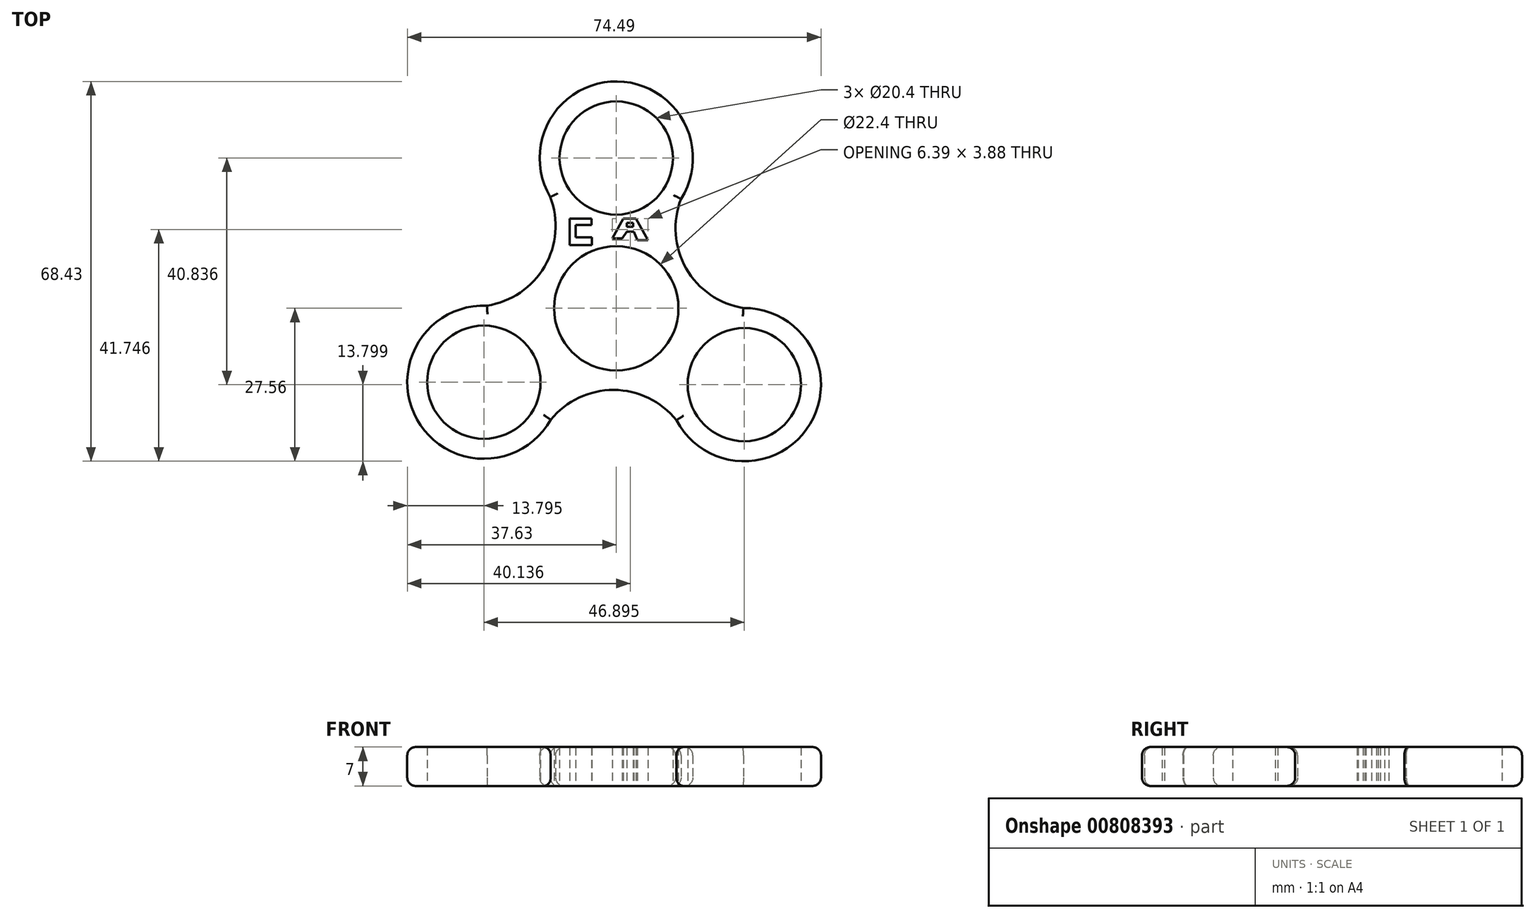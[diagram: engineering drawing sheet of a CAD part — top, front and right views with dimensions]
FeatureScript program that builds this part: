
annotation { "Feature Type Name" : "Feature", "Feature Type Description" : "" }
export const myFeature = defineFeature(function(context is Context, id is Id, definition is map)
    precondition{}
    {
        {
            var Q0;
            Q0=qCreatedBy(makeId("Top.planeOp"),FACE);
            var sketch = newSketch(context, id + "F0", { "sketchPlane" : qUnion([Q0])});
            skCircle(sketch, "E0", {"center": v(0, 0) * mm, "radius": 11.2 * mm});
            skCircle(sketch, "E1", {"center": v(0, 27.07) * mm, "radius": 10.2 * mm});
            skArc(sketch, "E2", {"start": v(11.66, 19.7) * mm, "mid": v(0.2, 40.87) * mm, "end": v(-11.87, 20.04) * mm});
            skArc(sketch, "E3.1.0", {"start": v(-23.27, 0.47) * mm, "mid": v(-35.89, -20.04) * mm, "end": v(-11.8, -20.08) * mm});
            skCircle(sketch, "E3.1.1", {"center": v(-23.83, -13.31) * mm, "radius": 10.2 * mm});
            skArc(sketch, "E3.2.0", {"start": v(10.84, -20.17) * mm, "mid": v(34.9, -20.84) * mm, "end": v(22.9, 0.04) * mm});
            skCircle(sketch, "E3.2.1", {"center": v(23.06, -13.76) * mm, "radius": 10.2 * mm});
            skPoint(sketch, "E3.center", {"position": v(-0.26, 0) * mm});
            skArc(sketch, "E4", {"start": v(12.88, 22.13) * mm, "mid": v(11.97, 8.4) * mm, "end": v(22.9, 0.04) * mm});
            skArc(sketch, "E5.1.0", {"start": v(-26, 0.32) * mm, "mid": v(-13.64, 6.39) * mm, "end": v(-11.87, 20.04) * mm});
            skArc(sketch, "E5.2.0", {"start": v(12.34, -22.45) * mm, "mid": v(0.9, -14.79) * mm, "end": v(-11.8, -20.08) * mm});
            skSolve(sketch);
        }
        {
            var Q0;
            Q0=qSketchRegion(id+"F0",true);
            extrude(context, id + "F1", {"entities" : qUnion([Q0]), "depth" : 7 * mm, "offsetDistance" : 25 * mm});
        }
        {
            var Q0;
            Q0=makeQuery(id+"F1.opExtrude","CAP_EDGE",EDGE,{"disambiguationData":[OSD([sQuery(id+"F0.wireOp",EDGE,"E2")])],"isStart":false});
            var Q1;
            Q1=makeQuery(id+"F1.opExtrude","CAP_EDGE",EDGE,{"disambiguationData":[OSD([sQuery(id+"F0.wireOp",EDGE,"E5.1.0")])],"isStart":false});
            var Q2;
            Q2=makeQuery(id+"F1.opExtrude","CAP_EDGE",EDGE,{"disambiguationData":[OSD([sQuery(id+"F0.wireOp",EDGE,"E3.1.0")])],"isStart":false});
            var Q3;
            Q3=makeQuery(id+"F1.opExtrude","CAP_EDGE",EDGE,{"disambiguationData":[OSD([sQuery(id+"F0.wireOp",EDGE,"E5.2.0")])],"isStart":false});
            var Q4;
            Q4=makeQuery(id+"F1.opExtrude","CAP_EDGE",EDGE,{"disambiguationData":[OSD([sQuery(id+"F0.wireOp",EDGE,"E3.2.0")])],"isStart":false});
            var Q5;
            Q5=makeQuery(id+"F1.opExtrude","CAP_EDGE",EDGE,{"disambiguationData":[OSD([sQuery(id+"F0.wireOp",EDGE,"E4")])],"isStart":false});
            var Q6;
            Q6=makeQuery(id+"F1.opExtrude","CAP_EDGE",EDGE,{"disambiguationData":[OSD([sQuery(id+"F0.wireOp",EDGE,"E2")])],"isStart":true});
            var Q7;
            Q7=makeQuery(id+"F1.opExtrude","CAP_EDGE",EDGE,{"disambiguationData":[OSD([sQuery(id+"F0.wireOp",EDGE,"E5.1.0")])],"isStart":true});
            var Q8;
            Q8=makeQuery(id+"F1.opExtrude","CAP_EDGE",EDGE,{"disambiguationData":[OSD([sQuery(id+"F0.wireOp",EDGE,"E3.1.0")])],"isStart":true});
            var Q9;
            Q9=makeQuery(id+"F1.opExtrude","CAP_EDGE",EDGE,{"disambiguationData":[OSD([sQuery(id+"F0.wireOp",EDGE,"E5.2.0")])],"isStart":true});
            var Q10;
            Q10=makeQuery(id+"F1.opExtrude","CAP_EDGE",EDGE,{"disambiguationData":[OSD([sQuery(id+"F0.wireOp",EDGE,"E3.2.0")])],"isStart":true});
            var Q11;
            Q11=makeQuery(id+"F1.opExtrude","CAP_EDGE",EDGE,{"disambiguationData":[OSD([sQuery(id+"F0.wireOp",EDGE,"E4")])],"isStart":true});
            fillet(context, id + "F2", {"entities" : qUnion([Q0, Q1, Q2, Q3, Q4, Q5, Q6, Q7, Q8, Q9, Q10, Q11]), "radius" : 1.5 * mm, "tangentPropagation" : true, "allowEdgeOverflow" : false});
        }
        {
            var Q0;
            Q0=qCreatedBy(makeId("Top.planeOp"),FACE);
            var sketch = newSketch(context, id + "F3", { "sketchPlane" : qUnion([Q0])});
            skLineSegment(sketch, "E6", {"start": v(-8.4, 16.13) * mm, "end": v(-8.4, 11.37) * mm});
            skLineSegment(sketch, "E7", {"start": v(-8.4, 11.37) * mm, "end": v(-4.4, 11.37) * mm});
            skLineSegment(sketch, "E8", {"start": v(-4.4, 11.37) * mm, "end": v(-4.4, 12.8) * mm});
            skLineSegment(sketch, "E9", {"start": v(-4.4, 12.8) * mm, "end": v(-7.3, 12.8) * mm});
            skLineSegment(sketch, "E10", {"start": v(-7.3, 12.8) * mm, "end": v(-7.3, 14.98) * mm});
            skLineSegment(sketch, "E11", {"start": v(-7.3, 14.98) * mm, "end": v(-4.46, 14.98) * mm});
            skLineSegment(sketch, "E12", {"start": v(-4.46, 14.98) * mm, "end": v(-4.46, 16.13) * mm});
            skLineSegment(sketch, "E13", {"start": v(-4.46, 16.13) * mm, "end": v(-8.4, 16.13) * mm});
            skLineSegment(sketch, "E14", {"start": v(1.28, 16.13) * mm, "end": v(3.57, 16.13) * mm});
            skLineSegment(sketch, "E15", {"start": v(3.57, 16.13) * mm, "end": v(5.7, 12.25) * mm});
            skLineSegment(sketch, "E16", {"start": v(5.7, 12.25) * mm, "end": v(3.79, 12.25) * mm});
            skLineSegment(sketch, "E17", {"start": v(3.79, 12.25) * mm, "end": v(3.19, 13.78) * mm});
            skLineSegment(sketch, "E18", {"start": v(3.19, 13.78) * mm, "end": v(1.88, 13.78) * mm});
            skLineSegment(sketch, "E19", {"start": v(1.88, 13.78) * mm, "end": v(1.06, 12.57) * mm});
            skLineSegment(sketch, "E20", {"start": v(1.06, 12.57) * mm, "end": v(-0.7, 12.57) * mm});
            skLineSegment(sketch, "E21", {"start": v(-0.7, 12.57) * mm, "end": v(1.28, 16.13) * mm});
            skLineSegment(sketch, "E22", {"start": v(1.88, 15.36) * mm, "end": v(3.02, 15.36) * mm});
            skLineSegment(sketch, "E23", {"start": v(3.02, 15.36) * mm, "end": v(3.02, 14.7) * mm});
            skLineSegment(sketch, "E24", {"start": v(3.02, 14.7) * mm, "end": v(1.88, 14.7) * mm});
            skLineSegment(sketch, "E25", {"start": v(1.88, 14.7) * mm, "end": v(1.88, 15.36) * mm});
            skSolve(sketch);
        }
        {
            var Q0;
            Q0=qSketchRegion(id+"F3",true);
            extrude(context, id + "F4", {"entities" : qUnion([Q0]), "operationType" : NewBodyOperationType.REMOVE, "depth" : 10 * mm, "offsetDistance" : 25 * mm});
        }
    });
